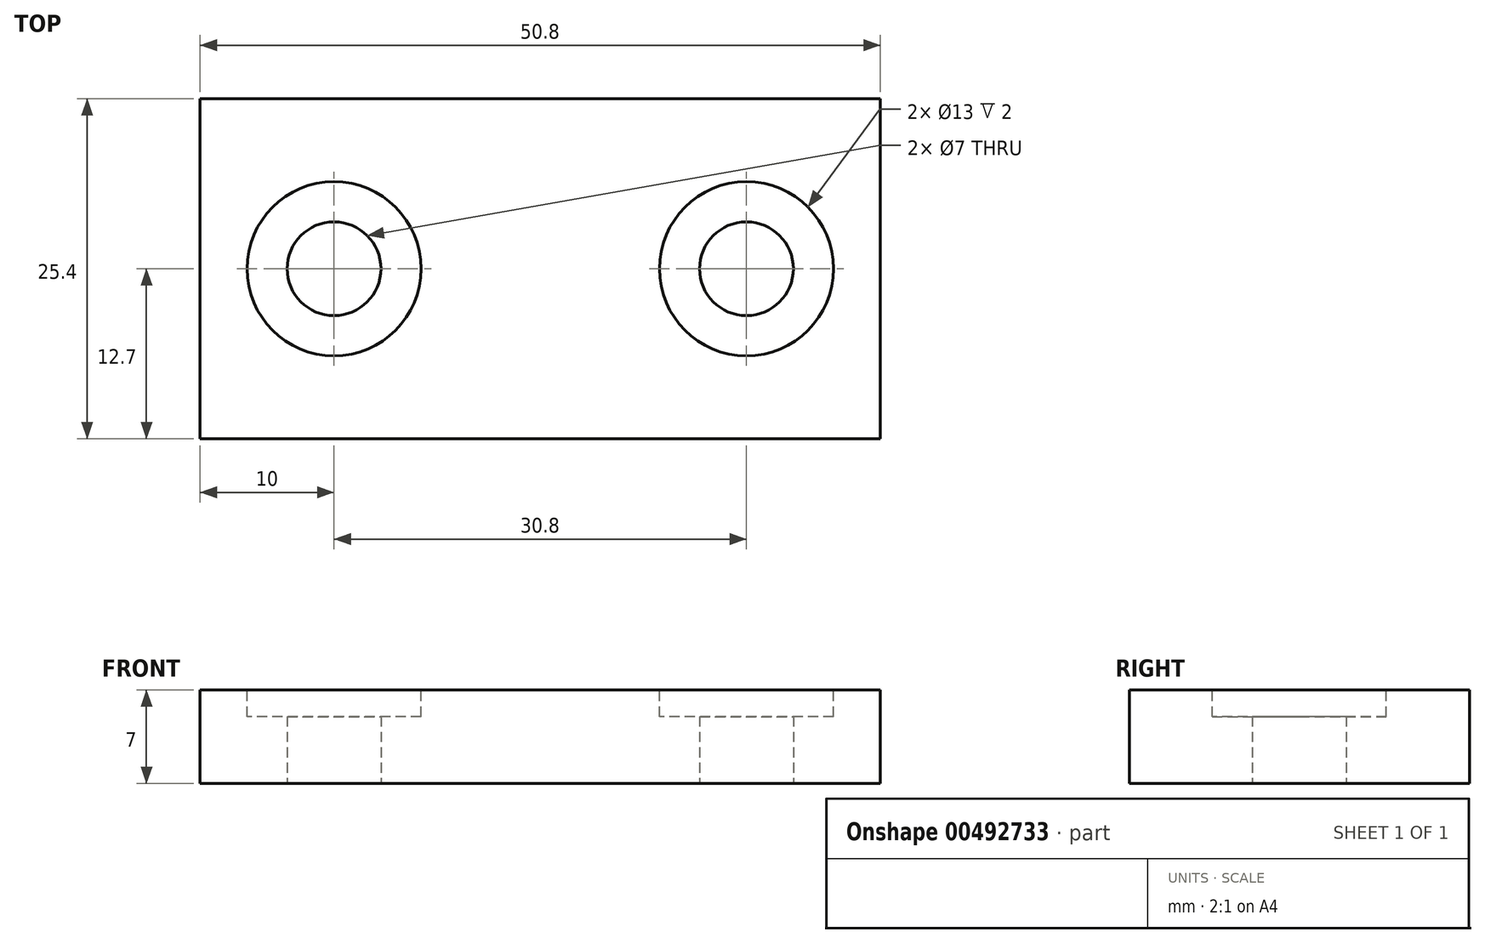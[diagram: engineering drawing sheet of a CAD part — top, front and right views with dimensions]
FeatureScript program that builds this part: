
annotation { "Feature Type Name" : "Feature", "Feature Type Description" : "" }
export const myFeature = defineFeature(function(context is Context, id is Id, definition is map)
    precondition{}
    {
        {
            var Q0;
            Q0=qCreatedBy(makeId("Top.planeOp"),FACE);
            var sketch = newSketch(context, id + "F0", { "sketchPlane" : qUnion([Q0])});
            skLineSegment(sketch, "E0.bottom", {"start": v(25.4, -12.7) * mm, "end": v(-25.4, -12.7) * mm});
            skLineSegment(sketch, "E0.top", {"start": v(25.4, 12.7) * mm, "end": v(-25.4, 12.7) * mm});
            skLineSegment(sketch, "E0.left", {"start": v(25.4, -12.7) * mm, "end": v(25.4, 12.7) * mm});
            skLineSegment(sketch, "E0.right", {"start": v(-25.4, -12.7) * mm, "end": v(-25.4, 12.7) * mm});
            skPoint(sketch, "E0.middle", {"position": v(0, 0) * mm});
            skSolve(sketch);
        }
        {
            var Q0;
            Q0=makeQuery(id+"F0.imprint","IMPRINT",FACE,{"disambiguationData":[TD([[makeQuery(id+"F0.imprint","IMPRINT",EDGE,{"derivedFrom":sQuery(id+"F0.wireOp",EDGE,"E0.bottom")}),-1.0]])]});
            extrude(context, id + "F1", {"entities" : qUnion([Q0]), "depth" : 7 * mm});
        }
        {
            var Q0;
            Q0=makeQuery(id+"F1.opExtrude","CAP_FACE",FACE,{"disambiguationData":[OSD([sQuery(id+"F0.wireOp",EDGE,"E0.bottom"),sQuery(id+"F0.wireOp",EDGE,"E0.top"),sQuery(id+"F0.wireOp",EDGE,"E0.left"),sQuery(id+"F0.wireOp",EDGE,"E0.right")])],"isStart":false});
            var sketch = newSketch(context, id + "F2", { "sketchPlane" : qUnion([Q0])});
            skCircle(sketch, "E1", {"center": v(-15.4, 0) * mm, "radius": 6.5 * mm});
            skPoint(sketch, "E1.centerSnap0", {"position": v(-25.4, 0) * mm});
            skCircle(sketch, "E2", {"center": v(15.4, 0) * mm, "radius": 6.5 * mm});
            skPoint(sketch, "E2.centerSnap0", {"position": v(25.4, 0) * mm});
            skSolve(sketch);
        }
        {
            var Q0;
            Q0=makeQuery(id+"F2.imprint","IMPRINT",FACE,{"disambiguationData":[TD([[makeQuery(id+"F2.imprint","IMPRINT",EDGE,{"derivedFrom":sQuery(id+"F2.wireOp",EDGE,"E1")}),1.0]])]});
            var Q1;
            Q1=makeQuery(id+"F2.imprint","IMPRINT",FACE,{"disambiguationData":[TD([[makeQuery(id+"F2.imprint","IMPRINT",EDGE,{"derivedFrom":sQuery(id+"F2.wireOp",EDGE,"E2")}),1.0]])]});
            extrude(context, id + "F3", {"entities" : qUnion([Q0, Q1]), "operationType" : NewBodyOperationType.REMOVE, "oppositeDirection" : true, "depth" : 2 * mm});
        }
        {
            var Q0;
            Q0=makeQuery(id+"F1.opExtrude","CAP_FACE",FACE,{"disambiguationData":[OSD([sQuery(id+"F0.wireOp",EDGE,"E0.bottom"),sQuery(id+"F0.wireOp",EDGE,"E0.top"),sQuery(id+"F0.wireOp",EDGE,"E0.left"),sQuery(id+"F0.wireOp",EDGE,"E0.right")])],"isStart":true});
            var sketch = newSketch(context, id + "F4", { "sketchPlane" : qUnion([Q0])});
            skCircle(sketch, "E3", {"center": v(-15.4, 0) * mm, "radius": 3.5 * mm});
            skCircle(sketch, "E4", {"center": v(15.4, 0) * mm, "radius": 3.5 * mm});
            skSolve(sketch);
        }
        {
            var Q0;
            Q0=makeQuery(id+"F4.imprint","IMPRINT",FACE,{"disambiguationData":[TD([[makeQuery(id+"F4.imprint","IMPRINT",EDGE,{"derivedFrom":sQuery(id+"F4.wireOp",EDGE,"E3")}),1.0]])]});
            var Q1;
            Q1=makeQuery(id+"F4.imprint","IMPRINT",FACE,{"disambiguationData":[TD([[makeQuery(id+"F4.imprint","IMPRINT",EDGE,{"derivedFrom":sQuery(id+"F4.wireOp",EDGE,"E4")}),1.0]])]});
            extrude(context, id + "F5", {"entities" : qUnion([Q0, Q1]), "operationType" : NewBodyOperationType.REMOVE, "oppositeDirection" : true, "depth" : 5 * mm});
        }
    });
